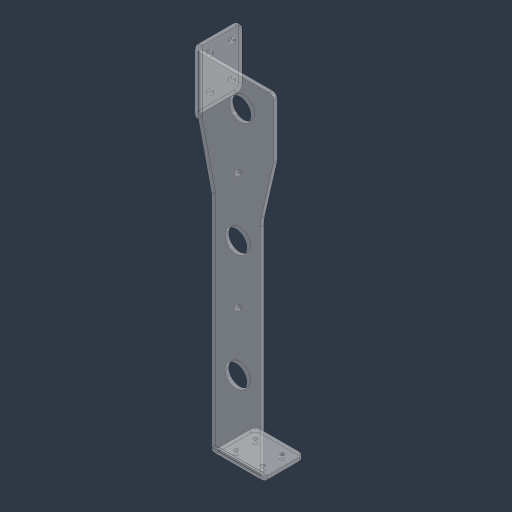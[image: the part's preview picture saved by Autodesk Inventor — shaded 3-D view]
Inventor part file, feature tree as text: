
AUTODESK INVENTOR PART (.ipt)
format: ipt  version: 2024.3 (Build 283343000, 343)  size: 259,584 bytes
history: native  units: in
note: dims shown in document units (in); Inventor stores cm internally (conversion verified against a paired STEP export)
features: sheet_metal_op x7, sketch x7, other x7, hole x4, chamfer x2, reference x2
ambient origin geometry x8: Origin, YZ Plane, XZ Plane, XY Plane, X Axis, Y Axis, Z Axis, Center Point
bodies: Solid1 (feature_tree)
feature tree (29):
  sheet_metal_op  "Face1"
  hole  "Hole1"  [1 undecoded]
  hole  "Hole2"  [1 undecoded]
  chamfer  "Corner Round1"
  sheet_metal_op  "Flange2"
  sheet_metal_op  "Flange3"
  hole  "Hole4"  [1 undecoded]
  hole  "Hole5"  [1 undecoded]
  chamfer  "Corner Round2"
  sketch  "Sketch1"  dims[d0=2.5in d1=11.6875in]
  other  "Plate1"
  sketch  "Sketch2"  dims[d2=3.1875in d3=6.0in]
  sketch  "Sketch3"  dims[d4=0.1875in d5=4.1875in]
  sketch  "Sketch5"  dims[d6=0.7874in d8=6.01in d9=0.3937in d11=1.0in]
  other  "Plate3"
  sheet_metal_op  "Bend2"
  sheet_metal_op  "Corner2"
  sketch  "Sketch7"  dims[d13=1.125in d14=0.75in d15=0.385in d16=0.25in d17=0.5635in d18=0.1875in d19=0.8108in]
  other  "Plate4"
  sheet_metal_op  "Bend3"
  sheet_metal_op  "Corner3"
  sketch  "Sketch8"  dims[d21=0.201in d22=0.75in d23=0.385in d24=0.25in d25=0.5635in d26=1.0in d27=0.8108in]
  sketch  "Sketch9"  dims[d29=1.25in d30=2.0in d43=3.0in d44=0.1875in d45=0.0938in d46=0.375in d47=0.1875in d48=2.0625in d49=90.0deg d50=0.1875in d51=0.75in d52=0.1875in d53=0.1875in d63=0.6875in d64=3.0in d65=0.1875in d66=0.0938in d67=0.375in d68=0.1875in d69=2.4375in d70=90.0deg d71=0.1875in d72=0.75in d73=0.1875in d74=0.1875in d75=1.75in d76=1.125in d77=0.625in d79=0.201in d80=0.75in d81=0.375in d82=0.25in d83=0.5635in d84=0.1875in d85=0.8108in d86=0.5625in d87=1.0in d88=1.375in d90=0.5625in d91=0.201in d92=0.75in d93=0.375in d94=0.25in d95=0.5635in d96=1.0in d97=0.8108in d98=6.01in d99=0.6047in d100=0.25in d101=0.5in]
  reference  "Reference1"
  reference  "Reference2"
  parser-record x1  (decoder bookkeeping rows leaked as tree rows — omitted from the tree; the rows remain in map.json)
  other  "#Poseidon 2025.iam"
  other  "feeder_bottom_plate:1"
  other  "Definition1"
note: 4 required parameter values undecoded (feature->parameter linkage not recoverable at this tier; creation-order binding heuristic only, values carry confidence <= 0.55)
note: 1 file-system path scrubbed to <path> (originals preserved in map.json)
